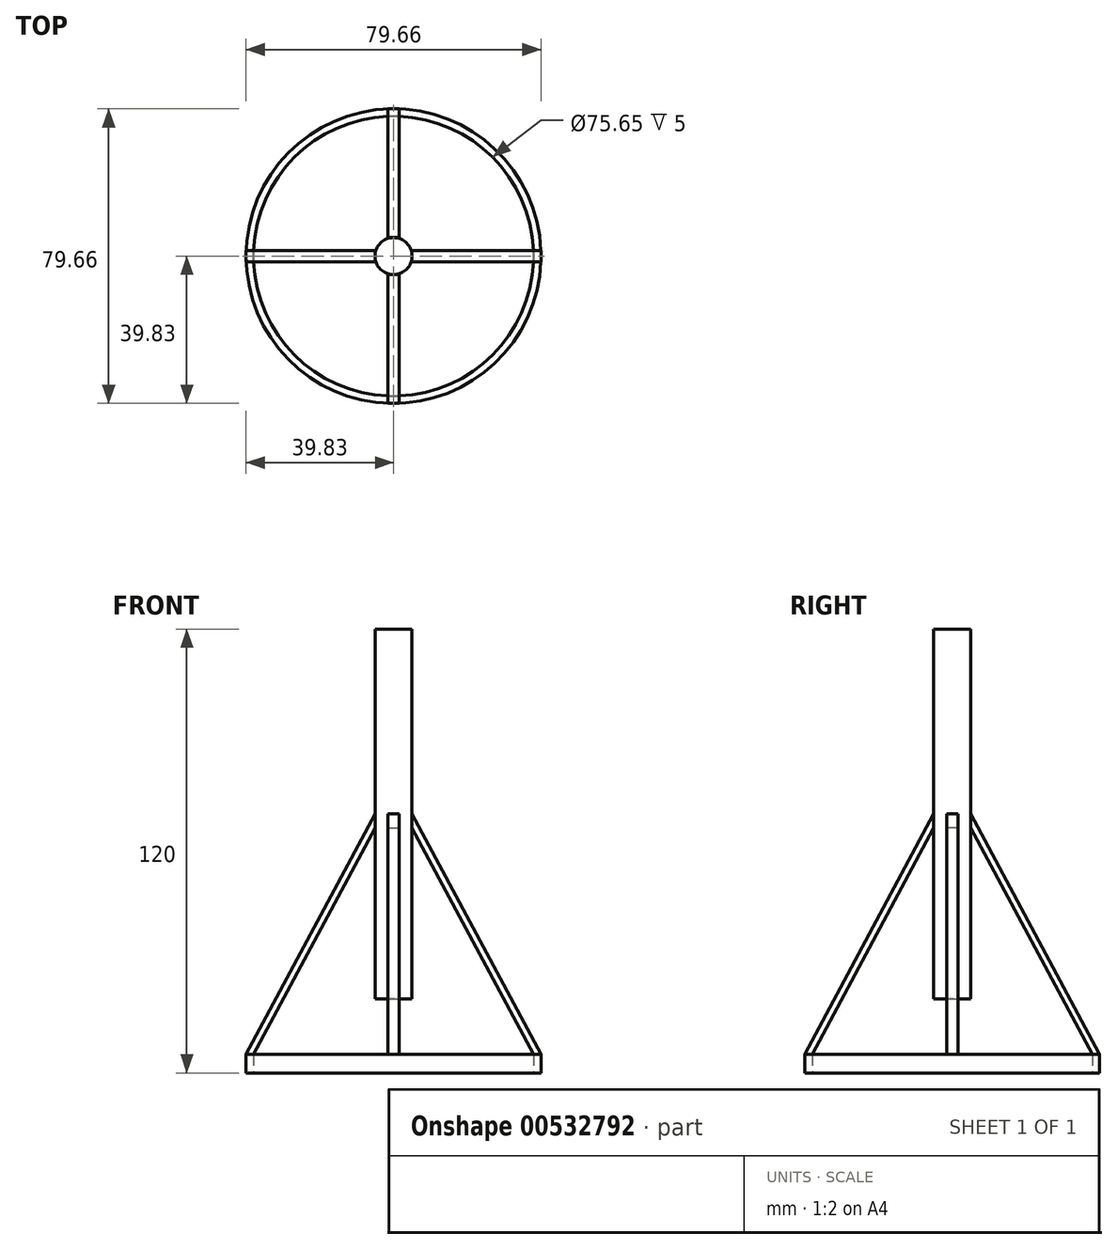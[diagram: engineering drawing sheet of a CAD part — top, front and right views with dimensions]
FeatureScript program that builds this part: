
annotation { "Feature Type Name" : "Feature", "Feature Type Description" : "" }
export const myFeature = defineFeature(function(context is Context, id is Id, definition is map)
    precondition{}
    {
        {
            var Q0;
            Q0=qCreatedBy(makeId("Top.planeOp"),FACE);
            var sketch = newSketch(context, id + "F0", { "sketchPlane" : qUnion([Q0])});
            skCircle(sketch, "E0", {"center": v(0, 0) * mm, "radius": 39.83 * mm});
            skCircle(sketch, "E1.0", {"center": v(0, 0) * mm, "radius": 37.83 * mm});
            skSolve(sketch);
        }
        {
            var Q0;
            Q0=makeQuery(id+"F0.imprint","IMPRINT",FACE,{"disambiguationData":[TD([[makeQuery(id+"F0.imprint","IMPRINT",EDGE,{"derivedFrom":sQuery(id+"F0.wireOp",EDGE,"E0")}),1.0]])]});
            extrude(context, id + "F1", {"entities" : qUnion([Q0]), "depth" : 5 * mm, "offsetDistance" : 25 * mm});
        }
        {
            var Q0;
            Q0=qCreatedBy(makeId("Top.planeOp"),FACE);
            cPlane(context, id + "F2", {"entities" : qUnion([Q0]), "cplaneType" : CPlaneType.OFFSET, "offset" : 20 * mm, "width" : 150 * mm, "height" : 150 * mm});
        }
        {
            var Q0;
            Q0=qCreatedBy(id+"F2.planeOp",FACE);
            var sketch = newSketch(context, id + "F3", { "sketchPlane" : qUnion([Q0])});
            skCircle(sketch, "E2", {"center": v(0, 0) * mm, "radius": 5 * mm});
            skSolve(sketch);
        }
        {
            var Q0;
            Q0=makeQuery(id+"F3.imprint","IMPRINT",FACE,{"disambiguationData":[TD([[makeQuery(id+"F3.imprint","IMPRINT",EDGE,{"derivedFrom":sQuery(id+"F3.wireOp",EDGE,"E2")}),1.0]])]});
            extrude(context, id + "F4", {"entities" : qUnion([Q0]), "depth" : 100 * mm, "offsetDistance" : 25 * mm});
        }
        {
            var Q0;
            Q0=qCreatedBy(makeId("Front.planeOp"),FACE);
            var sketch = newSketch(context, id + "F5", { "sketchPlane" : qUnion([Q0])});
            skLineSegment(sketch, "E3.0", {"start": v(-39.83, 5) * mm, "end": v(39.83, 5) * mm, "construction": true});
            skLineSegment(sketch, "E4", {"start": v(-39.83, 5) * mm, "end": v(-5, 70) * mm});
            skLineSegment(sketch, "E5", {"start": v(0, 0) * mm, "end": v(0, 20) * mm, "construction": true});
            skLineSegment(sketch, "E6.bottom", {"start": v(5, 20) * mm, "end": v(-5, 20) * mm, "construction": true});
            skLineSegment(sketch, "E6.top", {"start": v(5, 120) * mm, "end": v(-5, 120) * mm, "construction": true});
            skLineSegment(sketch, "E6.left", {"start": v(-5, 20) * mm, "end": v(-5, 120) * mm, "construction": true});
            skLineSegment(sketch, "E6.right", {"start": v(5, 20) * mm, "end": v(5, 120) * mm, "construction": true});
            skLineSegment(sketch, "E7", {"start": v(-39.83, 5) * mm, "end": v(-37.83, 5) * mm});
            skLineSegment(sketch, "E8", {"start": v(-37.83, 5) * mm, "end": v(-5, 66.27) * mm});
            skLineSegment(sketch, "E9", {"start": v(-5, 66.27) * mm, "end": v(-5, 70) * mm});
            skSolve(sketch);
        }
        {
            var Q0;
            Q0=makeQuery(id+"F5.imprint","IMPRINT",FACE,{"disambiguationData":[TD([[makeQuery(id+"F5.imprint","IMPRINT",EDGE,{"derivedFrom":sQuery(id+"F5.wireOp",EDGE,"E4")}),-1.0]])]});
            extrude(context, id + "F6", {"entities" : qUnion([Q0]), "endBound" : BoundingType.SYMMETRIC, "depth" : 3 * mm, "offsetDistance" : 25 * mm});
        }
        {
            var Q0;
            Q0=makeQuery(id+"F6.opExtrude","SWEPT_BODY",BODY,{"disambiguationData":[OSD([sQuery(id+"F5.wireOp",EDGE,"E4"),sQuery(id+"F5.wireOp",EDGE,"E7"),sQuery(id+"F5.wireOp",EDGE,"E8"),sQuery(id+"F5.wireOp",EDGE,"E9")])]});
            var Q1;
            Q1=makeQuery(id+"F4.opExtrude","CAP_EDGE",EDGE,{"disambiguationData":[OSD([sQuery(id+"F3.wireOp",EDGE,"E2")])],"isStart":true});
            circularPattern(context, id + "F7", {"entities" : qUnion([Q0]), "axis" : qUnion([Q1]), "angle" : 360 * degree, "instanceCount" : 4, "equalSpace" : true});
        }
    });
